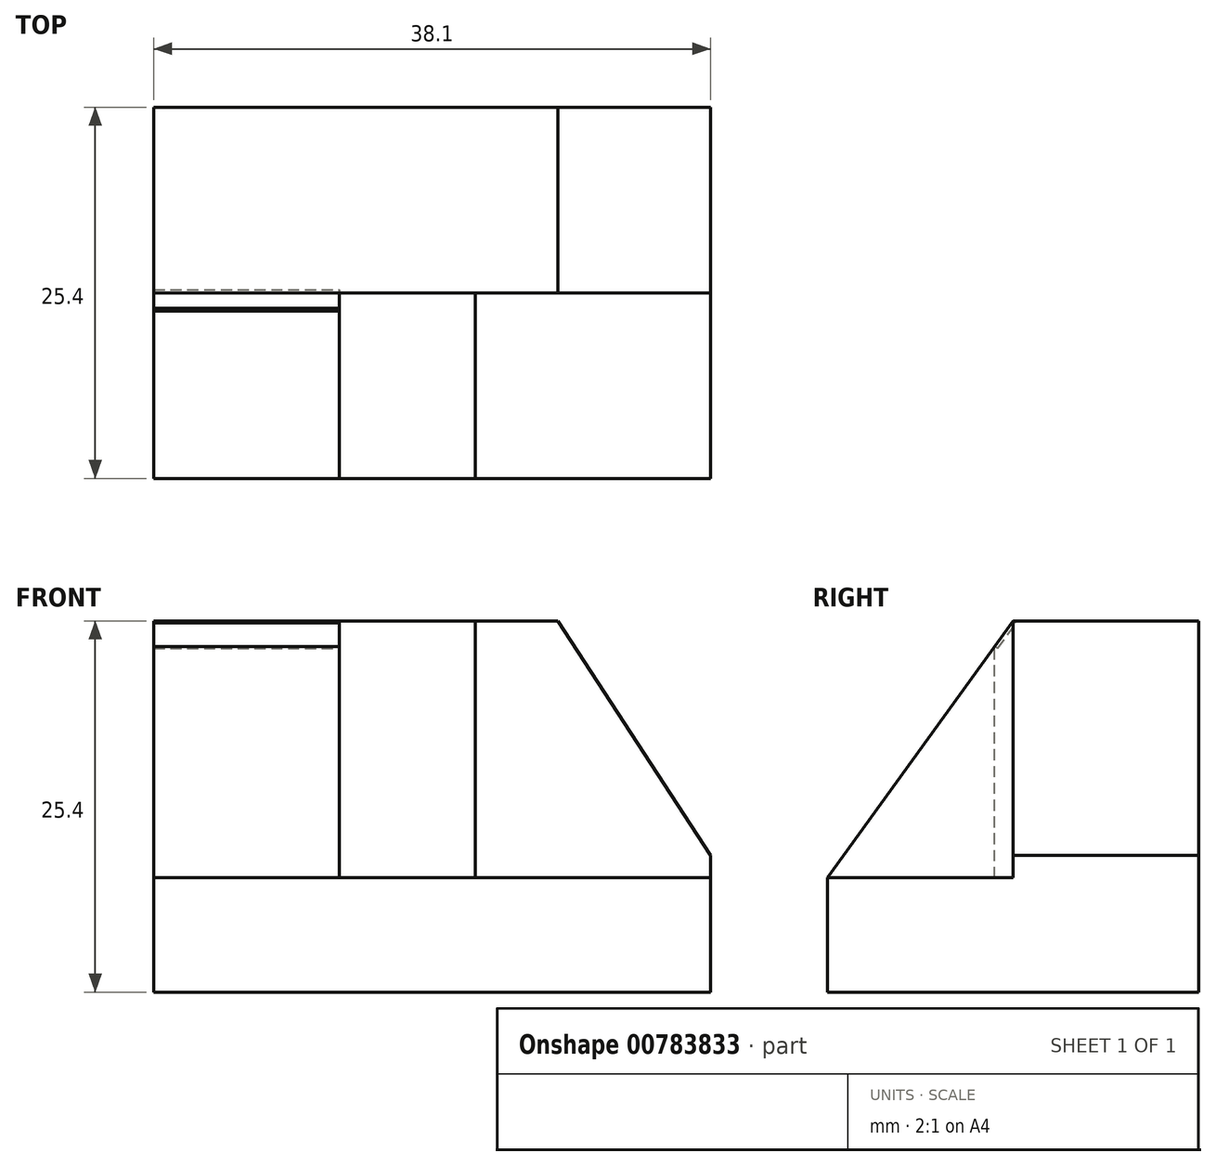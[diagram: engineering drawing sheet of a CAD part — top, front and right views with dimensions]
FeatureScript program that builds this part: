
annotation { "Feature Type Name" : "Feature", "Feature Type Description" : "" }
export const myFeature = defineFeature(function(context is Context, id is Id, definition is map)
    precondition{}
    {
        {
            var Q0;
            Q0=qCreatedBy(makeId("Front.planeOp"),FACE);
            var sketch = newSketch(context, id + "F0", { "sketchPlane" : qUnion([Q0])});
            skLineSegment(sketch, "E0", {"start": v(0, 25.4) * mm, "end": v(0, 0) * mm});
            skLineSegment(sketch, "E1", {"start": v(0, 0) * mm, "end": v(38.1, 0) * mm});
            skLineSegment(sketch, "E2", {"start": v(38.1, 0) * mm, "end": v(38.1, 25.4) * mm});
            skLineSegment(sketch, "E3", {"start": v(0, 25.4) * mm, "end": v(38.1, 25.4) * mm});
            skSolve(sketch);
        }
        {
            var Q0;
            Q0 = qSketchRegion(id + "F0", true);
            extrude(context, id + "F1", {"entities" : qUnion([Q0]), "depth" : 25.4 * mm, "offsetDistance" : 25.4 * mm});
        }
        {
            var Q0;
            Q0=makeQuery(id+"F1.opExtrude","CAP_FACE",FACE,{"disambiguationData":[OSD([sQuery(id+"F0.wireOp",EDGE,"E0"),sQuery(id+"F0.wireOp",EDGE,"E1"),sQuery(id+"F0.wireOp",EDGE,"E2"),sQuery(id+"F0.wireOp",EDGE,"E3")])],"isStart":false});
            var sketch = newSketch(context, id + "F2", { "sketchPlane" : qUnion([Q0])});
            skLineSegment(sketch, "E4", {"start": v(27.64, 25.4) * mm, "end": v(38.1, 9.35) * mm});
            skSolve(sketch);
        }
        {
            var Q0;
            Q0 = qSketchRegion(id + "F2", true);
            var Q1;
            {var subQ0=sQuery(id+"F2.wireOp",EDGE,"E4");Q1=makeQuery(id+"F2.imprint","IMPRINT",FACE,{"disambiguationData":[TD([[makeQuery(id+"F2.imprint","IMPRINT",EDGE,{"derivedFrom":subQ0}),1.0]])]});}
            extrude(context, id + "F3", {"entities" : qUnion([Q0, Q1]), "operationType" : NewBodyOperationType.REMOVE, "endBound" : BoundingType.THROUGH_ALL, "oppositeDirection" : true, "depth" : 25.4 * mm, "offsetDistance" : 25.4 * mm});
        }
        {
            var Q0;
            Q0=makeQuery(id+"F1.opExtrude","SWEPT_FACE",FACE,{"disambiguationData":[OSD([sQuery(id+"F0.wireOp",EDGE,"E0")])]});
            var sketch = newSketch(context, id + "F4", { "sketchPlane" : qUnion([Q0])});
            skLineSegment(sketch, "E5", {"start": v(25.4, 7.81) * mm, "end": v(13.96, 7.81) * mm});
            skLineSegment(sketch, "E6", {"start": v(13.96, 7.81) * mm, "end": v(13.96, 25.4) * mm});
            skSolve(sketch);
        }
        {
            var Q0;
            Q0 = qSketchRegion(id + "F4", true);
            var Q1;
            {var subQ0=sQuery(id+"F4.wireOp",EDGE,"E5");Q1=makeQuery(id+"F4.imprint","IMPRINT",FACE,{"disambiguationData":[TD([[makeQuery(id+"F4.imprint","IMPRINT",EDGE,{"derivedFrom":subQ0}),-1.0]])]});}
            extrude(context, id + "F5", {"entities" : qUnion([Q0, Q1]), "operationType" : NewBodyOperationType.REMOVE, "oppositeDirection" : true, "depth" : 12.7 * mm, "offsetDistance" : 25.4 * mm});
        }
        {
            var Q0;
            Q0=makeQuery(id+"F1.opExtrude","CAP_FACE",FACE,{"disambiguationData":[OSD([sQuery(id+"F0.wireOp",EDGE,"E0"),sQuery(id+"F0.wireOp",EDGE,"E1"),sQuery(id+"F0.wireOp",EDGE,"E2"),sQuery(id+"F0.wireOp",EDGE,"E3")])],"isStart":false});
            var sketch = newSketch(context, id + "F6", { "sketchPlane" : qUnion([Q0])});
            skLineSegment(sketch, "E7", {"start": v(12.7, 7.81) * mm, "end": v(38.1, 7.81) * mm});
            skPoint(sketch, "E7.endSnap0", {"position": v(38.1, 4.67) * mm});
            skLineSegment(sketch, "E8", {"start": v(38.1, 7.81) * mm, "end": v(38.1, 9.35) * mm});
            skLineSegment(sketch, "E9", {"start": v(38.1, 9.35) * mm, "end": v(27.64, 25.4) * mm});
            skLineSegment(sketch, "E10", {"start": v(27.64, 25.4) * mm, "end": v(22.01, 25.4) * mm});
            skLineSegment(sketch, "E11", {"start": v(22.01, 25.4) * mm, "end": v(22.01, 7.81) * mm});
            skPoint(sketch, "E11.endSnap0", {"position": v(25.4, 7.81) * mm});
            skSolve(sketch);
        }
        {
            var Q0;
            Q0 = qSketchRegion(id + "F6", true);
            extrude(context, id + "F7", {"entities" : qUnion([Q0]), "operationType" : NewBodyOperationType.REMOVE, "oppositeDirection" : true, "depth" : 12.7 * mm, "offsetDistance" : 25.4 * mm});
        }
        {
            var Q0;
            Q0=makeQuery(id+"F7.boolean.opBoolean","COPY",FACE,{"derivedFrom":makeQuery(id+"F7.opExtrude","SWEPT_FACE",FACE,{"disambiguationData":[OSD([sQuery(id+"F6.wireOp",EDGE,"E11")])]})});
            var sketch = newSketch(context, id + "F8", { "sketchPlane" : qUnion([Q0])});
            skLineSegment(sketch, "E12", {"start": v(-25.4, 7.81) * mm, "end": v(-12.7, 25.4) * mm});
            skSolve(sketch);
        }
        {
            var Q0;
            Q0 = qSketchRegion(id + "F8", true);
            var Q1;
            Q1=makeQuery(id+"F8.imprint","IMPRINT",FACE,{"disambiguationData":[TD([[makeQuery(id+"F8.imprint","IMPRINT",EDGE,{"derivedFrom":sQuery(id+"F8.wireOp",EDGE,"E12")}),1.0]])]});
            extrude(context, id + "F9", {"entities" : qUnion([Q0, Q1]), "operationType" : NewBodyOperationType.REMOVE, "oppositeDirection" : true, "depth" : 25.4 * mm, "offsetDistance" : 25.4 * mm});
        }
        {
            var Q0;
            Q0=makeQuery(id+"F9.boolean.opBoolean","COPY",FACE,{"derivedFrom":makeQuery(id+"F9.opExtrude","SWEPT_FACE",FACE,{"disambiguationData":[OSD([sQuery(id+"F8.wireOp",EDGE,"E12")])]})});
            var sketch = newSketch(context, id + "F10", { "sketchPlane" : qUnion([Q0])});
            skLineSegment(sketch, "E13", {"start": v(12.7, 11) * mm, "end": v(12.7, 13.16) * mm});
            skSolve(sketch);
        }
        {
            var Q0;
            Q0 = qSketchRegion(id + "F10", true);
            var Q1;
            {var subQ0=sQuery(id+"F10.wireOp",EDGE,"E13");Q1=makeQuery(id+"F10.imprint","IMPRINT",FACE,{"disambiguationData":[TD([[makeQuery(id+"F10.imprint","IMPRINT",EDGE,{"derivedFrom":subQ0}),1.0]])]});}
            extrude(context, id + "F11", {"entities" : qUnion([Q0, Q1]), "operationType" : NewBodyOperationType.REMOVE, "oppositeDirection" : true, "depth" : 0.25 * mm, "offsetDistance" : 25.4 * mm});
        }
    });
